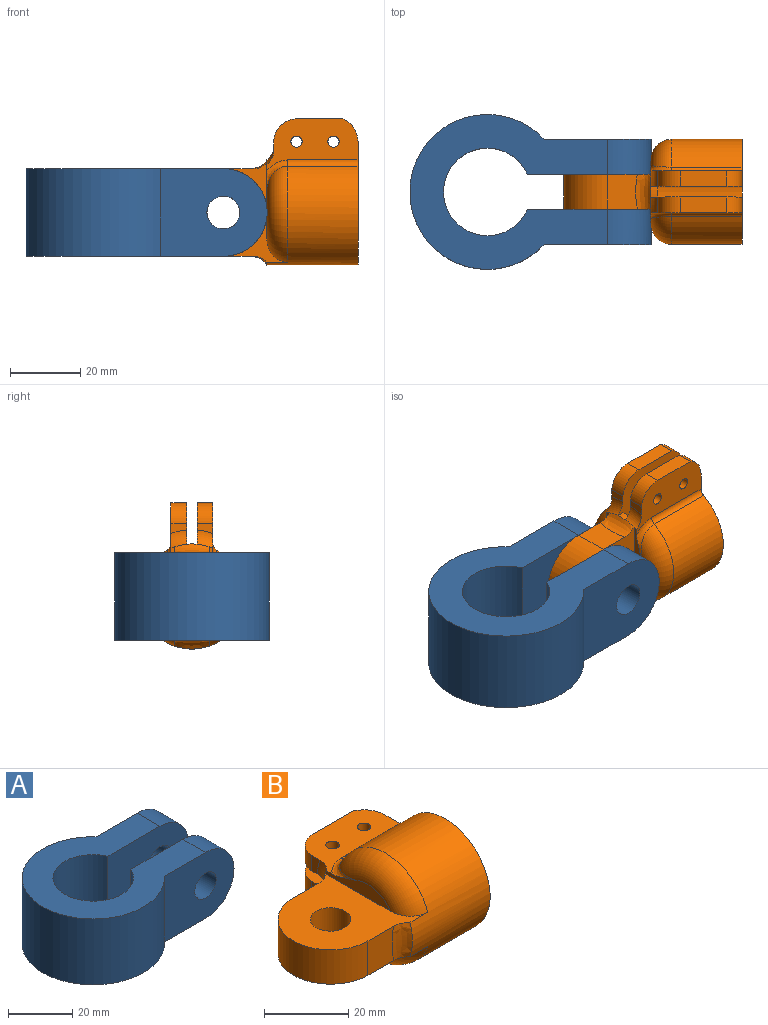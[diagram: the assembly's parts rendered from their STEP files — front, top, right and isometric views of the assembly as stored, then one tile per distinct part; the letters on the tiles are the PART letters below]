
ASSEMBLY  parts=2 mates=1
PART A: 16 faces, bbox 73.9x49.2x30 mm
  f0: plane 15x6.25mm, normal (1,0,0), area 8.3mm2, adj f4,f10,f14
  f1: plane 30.53x25mm, normal (0,-1,0), area 626.8mm2, adj f5,f6,f8,f11,f13,f15
  f2: plane 15x6.25mm, normal (1,0,0), area 8.3mm2, adj f3,f11,f15
  f3: plane 35.29x25mm, normal (0,1,0), area 746.1mm2, adj f2,f5,f6,f9,f11,f13,f15
  f4: plane 35.29x25mm, normal (0,-1,0), area 746.1mm2, adj f0,f5,f6,f9,f10,f12,f14
  f5: plane 56.36x44.2mm, normal (0,0,-1), area 1242.5mm2, adj f1,f3,f4,f7,f8,f9,f14,f15
  f6: plane 56.36x44.2mm, normal (0,0,1), area 1242.5mm2, adj f1,f3,f4,f7,f8,f9,f10,f11
  f7: plane 30.53x25mm, normal (0,1,0), area 626.8mm2, adj f5,f6,f8,f10,f12,f14
  f8: cylinder r=22.1mm len=44.2mm, axis (0,0,-1), area 2647.1mm2, adj f1,f5,f6,f7
  f9: cylinder r=12.5mm len=25mm, axis (0,0,-1), area 1706.3mm2, adj f3,f4,f5,f6
  f10: cylinder r=12.5mm len=12.5mm, axis (0,1,0), area 193.2mm2, adj f0,f4,f6,f7
  f11: cylinder r=12.5mm len=12.5mm, axis (0,1,0), area 193.2mm2, adj f1,f2,f3,f6
  f12: cylinder r=4.7mm len=10mm, axis (0,1,0), area 295.3mm2, adj f4,f7
  f13: cylinder r=4.7mm len=10mm, axis (0,1,0), area 295.3mm2, adj f1,f3
  f14: cylinder r=12.5mm len=12.5mm, axis (0,1,0), area 193.2mm2, adj f0,f4,f5,f7
  f15: cylinder r=12.5mm len=12.5mm, axis (0,1,0), area 193.2mm2, adj f1,f2,f3,f5
PART B: 39 faces, bbox 52.8x44x34.4 mm
  f0: plane 22.81x5.18mm, normal (-1,0,0), area 53.5mm2, adj f4,f14,f29,f33,f36
  f1: cylinder r=15mm len=30mm, axis (1,0,0), area 1651.8mm2, adj f9,f13,f14,f32,f33,f34,f35,f37
  f2: plane 4.5x2.74mm, normal (-1,0,0), area 9.8mm2, adj f4,f6,f25,f29
  f3: plane 4.5x2.74mm, normal (-1,0,0), area 9.8mm2, adj f7,f20,f23,f31
  f4: plane 26.04x14.91mm, normal (0,0,-1), area 254.1mm2, adj f0,f2,f5,f9,f25,f26,f27,f28
  f5: plane 13.18x4.5mm, normal (0,1,0), area 59.3mm2, adj f4,f6,f25,f26
  f6: plane 26.01x17.75mm, normal (0,0,1), area 395.3mm2, adj f2,f5,f9,f10,f17,f19,f25,f26
  f7: plane 26.01x17.75mm, normal (0,0,-1), area 395.3mm2, adj f3,f8,f9,f10,f17,f19,f21,f22
  f8: plane 13.18x4.5mm, normal (0,1,0), area 59.3mm2, adj f7,f20,f23,f24
  f9: plane 35.23x30mm, normal (1,0,0), area 481.4mm2, adj f1,f4,f6,f7,f19,f20,f24,f26
  f10: plane 24.1x18.2mm, normal (1,0,0), area 277.9mm2, adj f6,f7,f17,f19
  f11: plane 9.94x8.55mm, normal (0,1,0), area 81.7mm2, adj f13,f14,f15,f30
  f12: plane 9.94x8.55mm, normal (0,-1,0), area 81.7mm2, adj f13,f14,f15,f32
  f13: plane 32.84x30.25mm, normal (0,0,1), area 495.3mm2, adj f1,f11,f12,f15,f16,f18,f30,f32
  f14: plane 32.84x30.25mm, normal (0,0,-1), area 495.3mm2, adj f0,f1,f11,f12,f15,f16,f30,f32
  f15: cylinder r=12.5mm len=25mm, axis (0,0,-1), area 390.3mm2, adj f11,f12,f13,f14
  f16: cylinder r=4.8mm len=9.94mm, axis (0,0,-1), area 299.8mm2, adj f13,f14
  f17: cylinder r=15mm len=3mm, axis (1,0,0), area 6mm2, adj f6,f7,f10,f30
  f18: plane 22.81x5.18mm, normal (-1,0,0), area 53.5mm2, adj f13,f20,f31,f34,f38
  f19: cylinder r=9.1mm len=24mm, axis (-1,0,0), area 1299.9mm2, adj f6,f7,f9,f10
  f20: plane 26.05x14.92mm, normal (0,0,1), area 254.1mm2, adj f3,f8,f9,f18,f21,f22,f23,f24
  f21: cylinder r=1.6mm len=4.5mm, axis (0,0,1), area 45.2mm2, adj f7,f20
  f22: cylinder r=1.6mm len=4.5mm, axis (0,0,1), area 45.2mm2, adj f7,f20
  f23: cylinder r=6.48mm len=6.46mm, axis (0,0,1), area 43.4mm2, adj f3,f7,f8,f20
  f24: cylinder r=7mm len=6.48mm, axis (0,0,1), area 37.3mm2, adj f7,f8,f9,f20
  f25: cylinder r=6.48mm len=6.46mm, axis (0,0,1), area 43.4mm2, adj f2,f4,f5,f6
  f26: cylinder r=7mm len=6.48mm, axis (0,0,1), area 37.3mm2, adj f4,f5,f6,f9
  f27: cylinder r=1.6mm len=4.5mm, axis (0,0,1), area 45.2mm2, adj f4,f6
  f28: cylinder r=1.6mm len=4.5mm, axis (0,0,1), area 45.2mm2, adj f4,f6
  f29: torus R=19mm, axis (1,0,0), area 21.5mm2, adj f0,f2,f4,f6,f30
  f30: bspline ~12.29x4.33mm, area 49.3mm2, adj f11,f13,f14,f17,f29,f31
  f31: torus R=19mm, axis (1,0,0), area 21.5mm2, adj f3,f7,f18,f20,f30
  f32: bspline ~12.29x4.33mm, area 49.3mm2, adj f1,f12,f13,f14
  f33: torus R=9mm, axis (1,0,0), area 232.3mm2, adj f0,f1,f14,f36
  f34: torus R=9mm, axis (1,0,0), area 232.3mm2, adj f1,f13,f18,f38
  f35: cylinder r=2mm len=20mm, axis (1,0,0), area 43.2mm2, adj f1,f4,f9,f36
  f36: bspline ~12.08x8.72mm, area 22.8mm2, adj f0,f4,f33,f35
  f37: cylinder r=2mm len=20mm, axis (1,0,0), area 43.2mm2, adj f1,f9,f20,f38
  f38: bspline ~12.08x8.72mm, area 22.8mm2, adj f18,f20,f34,f37
PLACE A t=(-123.08,25.73,-5.84)mm
PLACE B rot(axis=(1,0,0),90deg) t=(-88.81,25.76,6.65)mm
MATE revolute B.f16 <-> A.f12  axis (0,1,0) through (-88.81,30.73,6.65)mm
